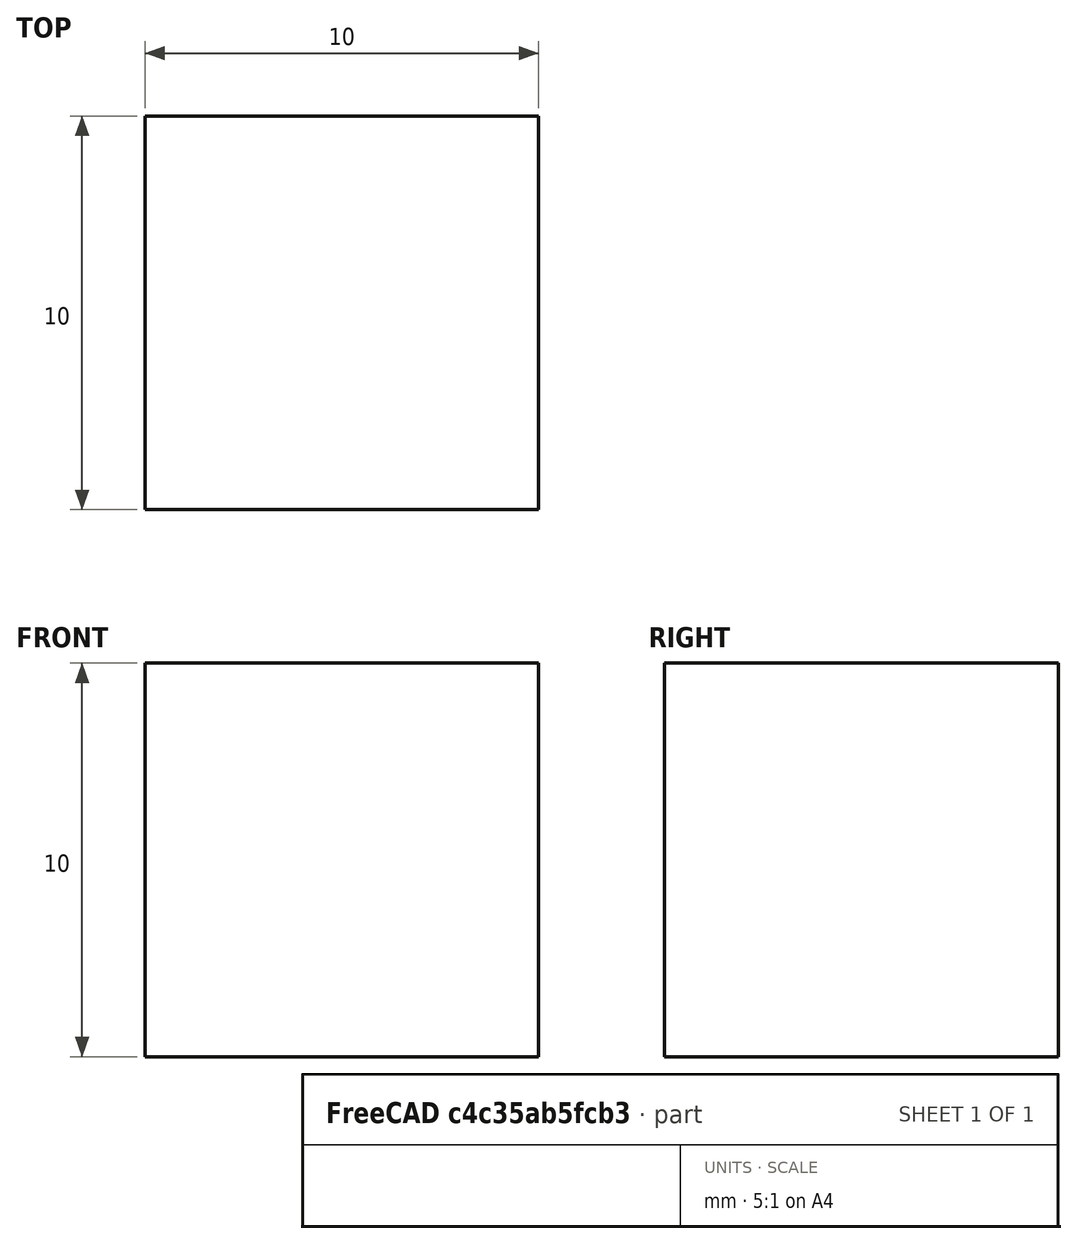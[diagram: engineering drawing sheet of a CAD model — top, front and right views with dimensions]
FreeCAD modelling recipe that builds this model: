
FCSTD DOCUMENT  (FreeCAD 0.21R33771 (Git))
Label: tensile
License: All rights reserved
LicenseURL: http://en.wikipedia.org/wiki/All_rights_reserved
objects: Fem::FemMeshObjectPython×3, Fem::ConstraintDisplacement×3, Fem::FemResultObjectPython×2, Part::Box×1, Fem::ConstraintForce×1, App::MaterialObjectPython×1, Fem::FemSolverObjectPython×1, Fem::FemAnalysis×1
note: 1 computed .brp shape members not serialized (recipe doc carries the construction recipe); baked Part::Feature solids carry a one-line shape summary decoded from their .brp

FEATURE [Part::Box] Box  label="Cube"
  AttacherType = Attacher::AttachEngine3D
  Height = 10
  Length = 10
  Width = 10
FEATURE [Fem::FemMeshObjectPython] FEMMeshGmsh  # FEM object (typed FeaturePython)
  Algorithm2D = 0
  Algorithm3D = 0
  CharacteristicLengthMax = 10
  CharacteristicLengthMin = 10
  CoherenceMesh = true
  ElementDimension = 0
  ElementOrder = 1
  GeometryTolerance = 1e-06
  GroupsOfNodes = false
  HighOrderOptimize = 0
  MeshSizeFromCurvature = 12
  OptimizeNetgen = false
  OptimizeStd = true
  Part = -> Box
  RecombinationAlgorithm = 0
  Recombine3DAll = false
  RecombineAll = false
  SecondOrderLinear = false
FEATURE [Fem::ConstraintForce] ConstraintForce
  DirectionVector = (0,0,1)
  Force = 100000
  NormalDirection = (0,0,1)
  Points = (9) [(0,0,10),(5,0,10),(10,0,10),(0,5,10),(5,5,10),(10,5,10),(0,10,10),(5,10,10),(10,10,10)]
  References = -> [Box]
FEATURE [Fem::ConstraintDisplacement] ConstraintDisplacement
  NormalDirection = (0,0,-1)
  Normals = (9) [(0,0,-1),(0,0,-1),(0,0,-1),(0,0,-1),(0,0,-1),(0,0,-1),(0,0,-1),(0,0,-1),(0,0,-1)]
  Points = (9) [(0,0,0),(5,0,0),(10,0,0),(0,5,0),(5,5,0),(10,5,0),(0,10,0),(5,10,0),(10,10,0)]
  References = -> [Box]
  hasXFormula = false
  hasYFormula = false
  hasZFormula = false
  rotxFix = false
  rotxFree = true
  rotyFix = false
  rotyFree = true
  rotzFix = false
  rotzFree = true
  useFlowSurfaceForce = false
  xDisplacement = 0
  xFix = false
  xFree = true
  xRotation = 0
  yDisplacement = 0
  yFix = false
  yFree = true
  yRotation = 0
  zDisplacement = 0
  zFix = false
  zFree = false
  zRotation = 0
FEATURE [Fem::ConstraintDisplacement] ConstraintDisplacement001
  NormalDirection = (0,-1,0)
  Normals = (9) [(0,-1,0),(0,-1,0),(0,-1,0),(0,-1,0),(0,-1,0),(0,-1,0),(0,-1,0),(0,-1,0),(0,-1,0)]
  Points = (9) [(0,0,0),(0,0,5),(0,0,10),(5,0,0),(5,0,5),(5,0,10),(10,0,0),(10,0,5),(10,0,10)]
  References = -> [Box]
  hasXFormula = false
  hasYFormula = false
  hasZFormula = false
  rotxFix = false
  rotxFree = true
  rotyFix = false
  rotyFree = true
  rotzFix = false
  rotzFree = true
  useFlowSurfaceForce = false
  xDisplacement = 0
  xFix = false
  xFree = true
  xRotation = 0
  yDisplacement = 0
  yFix = false
  yFree = false
  yRotation = 0
  zDisplacement = 0
  zFix = false
  zFree = true
  zRotation = 0
FEATURE [Fem::ConstraintDisplacement] ConstraintDisplacement002
  NormalDirection = (-1,0,0)
  Normals = (9) [(-1,0,0),(-1,0,0),(-1,0,0),(-1,0,0),(-1,0,0),(-1,0,0),(-1,0,0),(-1,0,0),(-1,0,0)]
  Points = (9) [(0,10,0),(0,10,5),(0,10,10),(0,5,0),(0,5,5),(0,5,10),(0,0,0),(0,0,5),(0,0,10)]
  References = -> [Box]
  hasXFormula = false
  hasYFormula = false
  hasZFormula = false
  rotxFix = false
  rotxFree = true
  rotyFix = false
  rotyFree = true
  rotzFix = false
  rotzFree = true
  useFlowSurfaceForce = false
  xDisplacement = 0
  xFix = false
  xFree = false
  xRotation = 0
  yDisplacement = 0
  yFix = false
  yFree = true
  yRotation = 0
  zDisplacement = 0
  zFix = false
  zFree = true
  zRotation = 0
FEATURE [App::MaterialObjectPython] MaterialSolid  # material (typed FeaturePython)
  Category = 0
  Material = AuthorAndLicense=(c) 2014 M. Münch - GNU Lesser General Public License (LGPL),CardName=Steel-S340MC,Density=7800 kg/m^3,+15 more (map truncated)
FEATURE [Fem::FemSolverObjectPython] SolverCcxTools  # FEM object (typed FeaturePython)
  AnalysisType = 0
  BeamShellResultOutput3D = false
  BucklingFactors = 1
  EigenmodeHighLimit = 1000000
  EigenmodeLowLimit = 0
  EigenmodesCount = 10
  GeometricalNonlinearity = 0
  IterationsControlParameterCutb = 0.25,0.5,0.75,0.85,,,1.5,
  IterationsControlParameterIter = 4,8,9,200,10,400,,200,,
  IterationsControlParameterTimeUse = false
  IterationsThermoMechMaximum = 2000
  IterationsUserDefinedIncrementations = false
  IterationsUserDefinedTimeStepLength = false
  MaterialNonlinearity = 0
  MatrixSolverType = 0
  SplitInputWriter = false
  ThermoMechSteadyState = true
  TimeEnd = 1
  TimeInitialStep = 0.01
FEATURE [Fem::FemMeshObjectPython] Result_Mesh_Volume  # FEM object (typed FeaturePython)
FEATURE [Fem::FemResultObjectPython] ResultMechanical  label="ElasticPlasticDisplacementResults"  # FEM object (typed FeaturePython)
  CriticalStrainRatio = [0.0735161,0.0735161,0.0735161,0.0735161,0.0735161,0.0735161,0.0735161,0.0735161,0.0735161,0.0735161,0.0735161,0.0735161,0.0735161,0.0735161,0.0735161,0.0735161,0.0735161,0.0735161,0.0735161,0.0735161,0.0735161,0.0735161,0.0735161,0.0735161,+39 more]
  DisplacementLengths = [0.23379,0,0.251202,0.0918946,0.251202,0.0918946,0.267483,0.129959,0.116895,0.238263,0.148691,0.0459473,0.148691,0.25537,0.174796,0.102741,0.0459473,0.238263,0.102741,0.25537,0.125601,0.176841,0.0628006,0.188402,0.0903672,0.155629,0.111304,+36 more]
  DisplacementVectors = (63) [(0,0,0.23379),(0,0,0),(0,-0.0918946,0.23379),(0,-0.0918946,0),(-0.0918946,0,0.23379),(-0.0918946,0,0),(-0.0918946,-0.0918946,0.23379),+56 more]
  Eigenmode = 0
  EigenmodeFrequency = 0
  Mesh = -> Result_Mesh_Volume
  NodeNumbers = [1,2,3,4,5,6,7,8,9,10,11,12,13,14,15,16,17,18,19,20,21,22,23,24,25,26,27,28,29,30,31,32,33,34,35,36,37,38,39,40,41,42,43,44,45,46,47,48,49,50,51,52,53,54,55,56,57,58,59,60,61,62,63]
  NodeStressXX = [0.00375951,0.00375951,0.00375951,0.00375951,0.00375951,0.00375951,0.00375951,0.00375951,0.00375951,0.00375951,0.00375951,0.00375951,0.00375951,0.00375951,0.00375951,0.00375951,0.00375951,0.00375951,0.00375951,0.00375951,0.00375951,+42 more]
  NodeStressXY = [2.69855e-14,-3.0474e-14,-2.35053e-13,-1.43885e-14,1.29623e-13,-3.29585e-14,-9.59207e-13,5.83268e-14,-1.74426e-15,-1.04034e-13,-1.24721e-13,-2.24313e-14,4.83323e-14,-4.14792e-13,-4.5044e-13,1.26842e-14,-3.17163e-14,7.83043e-14,2.19692e-14,+44 more]
  NodeStressXZ = [-3.82279e-13,1.7993e-13,1.2181e-13,-9.87094e-14,2.04953e-13,-5.15708e-13,7.81255e-13,-1.10767e-14,-1.01175e-13,-1.30235e-13,1.15504e-14,4.06102e-14,-1.55378e-13,4.93104e-13,3.85089e-13,-2.63392e-13,-1.67889e-13,-8.86633e-14,-5.4893e-14,+44 more]
  NodeStressYY = [0.00375951,0.00375951,0.00375951,0.00375951,0.00375951,0.00375951,0.00375951,0.00375951,0.00375951,0.00375951,0.00375951,0.00375951,0.00375951,0.00375951,0.00375951,0.00375951,0.00375951,0.00375951,0.00375951,0.00375951,0.00375951,+42 more]
  NodeStressYZ = [-1.61966e-13,-1.88499e-13,2.86462e-13,-1.09273e-13,-1.7024e-13,-3.7868e-14,5.29209e-13,-3.08604e-13,-1.75232e-13,6.22481e-14,8.85947e-14,-1.48886e-13,-1.04054e-13,1.79485e-13,1.10302e-13,-1.73236e-13,-1.13183e-13,-1.66103e-13,-2.08939e-13,+44 more]
  NodeStressZZ = [500.004,500.004,500.004,500.004,500.004,500.004,500.004,500.004,500.004,500.004,500.004,500.004,500.004,500.004,500.004,500.004,500.004,500.004,500.004,500.004,500.004,500.004,500.004,500.004,500.004,500.004,500.004,500.004,500.004,500.004,+33 more]
  Peeq = [0.018379,0.018379,0.018379,0.018379,0.018379,0.018379,0.018379,0.018379,0.018379,0.018379,0.018379,0.018379,0.018379,0.018379,0.018379,0.018379,0.018379,0.018379,0.018379,0.018379,0.018379,0.018379,0.018379,0.018379,0.018379,0.018379,+37 more]
  ResultType = Fem::ResultMechanical
  Stats = [-0.0918946,0,-0.0918946,0,0,0.23379,0,0.267483,500,500,0,0,0,0,0,0,0,0,0.018379,0.018379,0.0735161,0.0735161,0,0,0,0]
  Temperature = [0.0735161,0.0735161,0.0735161,0.0735161,0.0735161,0.0735161,0.0735161,0.0735161,0.0735161,0.0735161,0.0735161,0.0735161,0.0735161,0.0735161,0.0735161,0.0735161,0.0735161,0.0735161,0.0735161,0.0735161,0.0735161,0.0735161,0.0735161,0.0735161,+39 more]
  Time = 0
  vonMises = [500,500,500,500,500,500,500,500,500,500,500,500,500,500,500,500,500,500,500,500,500,500,500,500,500,500,500,500,500,500,500,500,500,500,500,500,500,500,500,500,500,500,500,500,500,500,500,500,500,500,500,500,500,500,500,500,500,500,500,500,+3 more]
FEATURE [Fem::FemMeshObjectPython] Result_Mesh_Volume001  # FEM object (typed FeaturePython)
FEATURE [Fem::FemResultObjectPython] ResultMechanical001  label="ElasticDisplacementResults"  # FEM object (typed FeaturePython)
  DisplacementLengths = [0.1,0,0.1,3.39958e-17,0.1,3.02188e-17,0.1,7.3716e-18,0.05,0.1,0.05,1.80595e-17,0.05,0.1,0.05,2.75863e-17,1.67695e-17,0.1,1.97757e-17,0.1,0.05,0.075,0.025,0.075,0.025,0.05,0.025,0.075,0.075,0.025,0.05,0.025,0.075,0.075,0.025,0.05,0.075,+26 more]
  DisplacementVectors = (63) [(0,0,0.1),(0,0,0),(0,-1.21075e-16,0.1),(0,3.39958e-17,0),(1.9147e-17,0,0.1),(-3.02188e-17,0,0),(2.26132e-17,-1.21874e-16,0.1),+56 more]
  Eigenmode = 0
  EigenmodeFrequency = 0
  Mesh = -> Result_Mesh_Volume001
  NodeNumbers = [1,2,3,4,5,6,7,8,9,10,11,12,13,14,15,16,17,18,19,20,21,22,23,24,25,26,27,28,29,30,31,32,33,34,35,36,37,38,39,40,41,42,43,44,45,46,47,48,49,50,51,52,53,54,55,56,57,58,59,60,61,62,63]
  ResultType = Fem::ResultMechanical
  Stats = [-3.02188e-17,5.53813e-17,-1.21874e-16,3.39958e-17,0,0.1,0,0.1,0,0,0,0,0,0,0,0,0,0,0,0,0,0,0,0,0,0]
  Time = 0
FEATURE [Fem::FemAnalysis] Analysis
  Group = -> [FEMMeshGmsh,ConstraintForce,ConstraintDisplacement,ConstraintDisplacement001,ConstraintDisplacement002,MaterialSolid,SolverCcxTools,ResultMechanical,ResultMechanical001]
